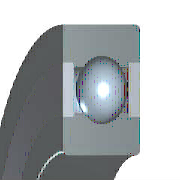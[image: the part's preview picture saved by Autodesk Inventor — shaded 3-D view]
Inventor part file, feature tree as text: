
AUTODESK INVENTOR PART (.ipt)
format: ipt  version: 2017 SP1 (Build 210196100, 196)  size: 309,760 bytes
history: native  units: mm (DEFAULTED — no unit token found)
features: sketch x1, other x1, pattern_circular x1
ambient origin geometry x8: Origin, YZ Plane, XZ Plane, XY Plane, X Axis, Y Axis, Z Axis, Center Point
bodies: Solid1 (feature_tree), Body (feature_tree)
feature tree (3):
  sketch  "Sketch"  dims[d0=2.86mm d17=90.0deg d18=90.0deg d1=0.3mm d2=60.0mm d3=360.0deg d4=0.0mm d5=0.0mm d6=0.0mm d7=6.0mm d8=17.0mm d9=11.5mm d10=17.0mm d11=9.1067mm d12=9.1067mm d13=9.586mm d14=1.0mm d15=5.0mm d16=6.0mm d19=1.0mm d20=2.0mm d22=3.0mm d23=0.0mm d24=0.0mm]
  other  "Ball"
  pattern_circular  "Balls"  Angle=90.0deg  [1 undecoded]
note: 1 required parameter value undecoded (feature->parameter linkage not recoverable at this tier; creation-order binding heuristic only, values carry confidence <= 0.55)
